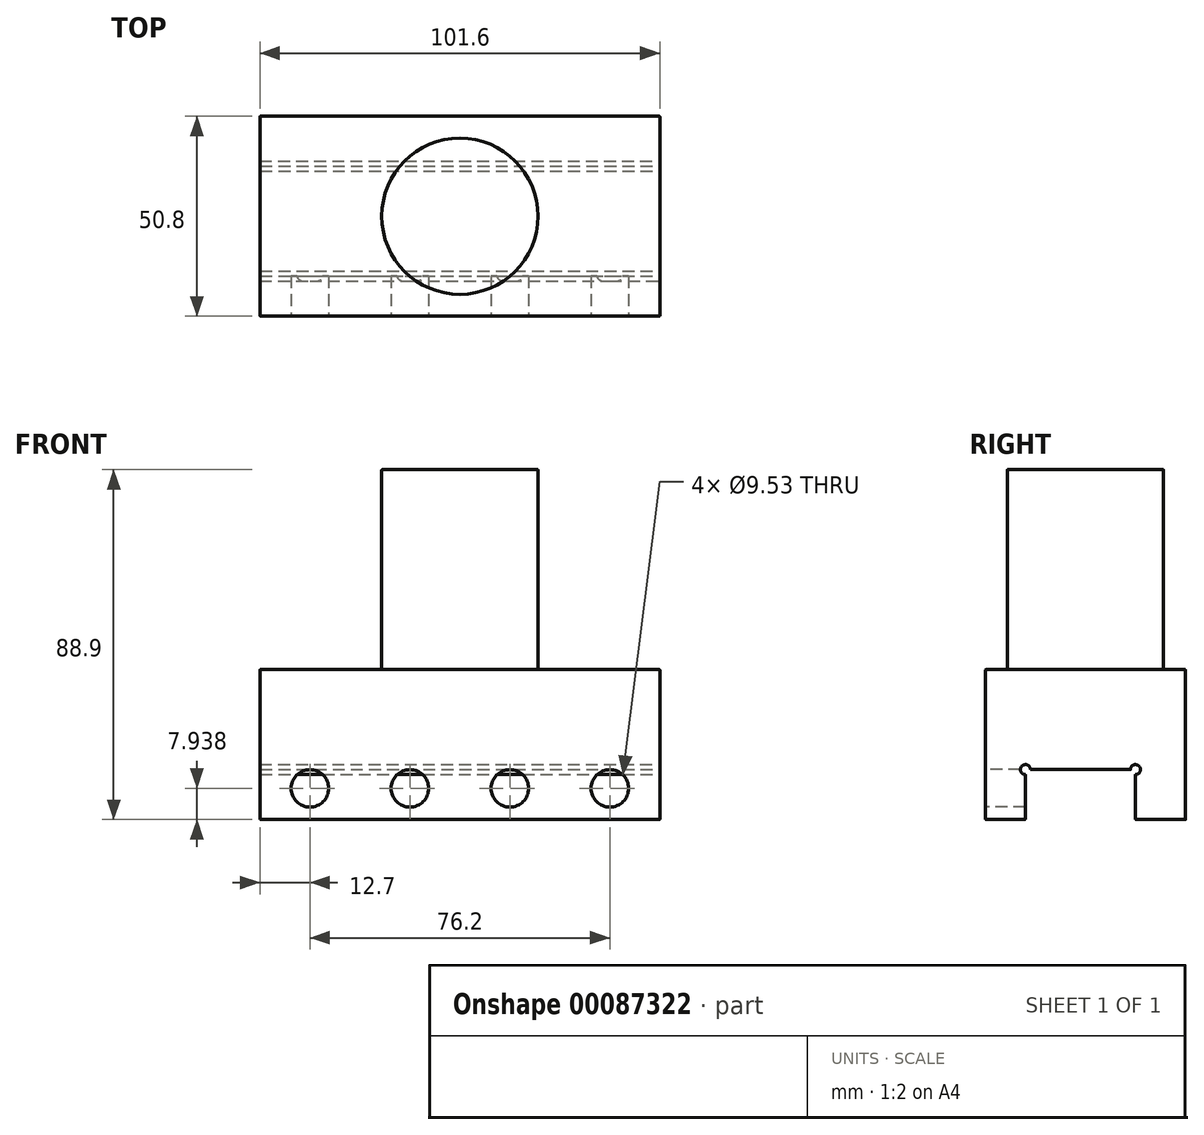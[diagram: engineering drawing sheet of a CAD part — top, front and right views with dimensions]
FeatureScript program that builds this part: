
annotation { "Feature Type Name" : "Feature", "Feature Type Description" : "" }
export const myFeature = defineFeature(function(context is Context, id is Id, definition is map)
    precondition{}
    {
        {
            var Q0;
            Q0=qCreatedBy(makeId("Right.planeOp"),FACE);
            var sketch = newSketch(context, id + "F0", { "sketchPlane" : qUnion([Q0])});
            skLineSegment(sketch, "E0", {"start": v(0, 0) * mm, "end": v(0, 38.1) * mm});
            skLineSegment(sketch, "E1", {"start": v(0, 38.1) * mm, "end": v(50.8, 38.1) * mm});
            skLineSegment(sketch, "E2", {"start": v(50.8, 38.1) * mm, "end": v(50.8, 0) * mm});
            skLineSegment(sketch, "E3", {"start": v(50.8, 0) * mm, "end": v(38.1, 0) * mm});
            skLineSegment(sketch, "E4", {"start": v(38.1, 0) * mm, "end": v(38.1, 11.43) * mm});
            skLineSegment(sketch, "E5", {"start": v(36.83, 12.7) * mm, "end": v(11.43, 12.7) * mm});
            skLineSegment(sketch, "E6", {"start": v(10.16, 11.43) * mm, "end": v(10.16, 0) * mm});
            skLineSegment(sketch, "E7", {"start": v(10.16, 0) * mm, "end": v(0, 0) * mm});
            skArc(sketch, "E8", {"start": v(11.43, 12.7) * mm, "mid": v(9.26, 13.6) * mm, "end": v(10.16, 11.43) * mm});
            skArc(sketch, "E9", {"start": v(38.1, 11.43) * mm, "mid": v(39, 13.6) * mm, "end": v(36.83, 12.7) * mm});
            skSolve(sketch);
        }
        {
            var Q0;
            Q0 = qSketchRegion(id + "F0", true);
            extrude(context, id + "F1", {"entities" : qUnion([Q0]), "oppositeDirection" : true, "depth" : 101.6 * mm});
        }
        {
            var Q0;
            Q0=makeQuery(id+"F1.opExtrude","SWEPT_FACE",FACE,{"disambiguationData":[OSD([sQuery(id+"F0.wireOp",EDGE,"E1")])]});
            var sketch = newSketch(context, id + "F2", { "sketchPlane" : qUnion([Q0])});
            skCircle(sketch, "E10", {"center": v(-50.8, 25.4) * mm, "radius": 19.84 * mm});
            skLineSegment(sketch, "E11", {"start": v(-50.8, 25.4) * mm, "end": v(0, 25.4) * mm});
            skLineSegment(sketch, "E12", {"start": v(-50.8, 25.4) * mm, "end": v(-101.6, 25.4) * mm});
            skPoint(sketch, "E12.endSnap0", {"position": v(-101.6, 25.4) * mm});
            skLineSegment(sketch, "E13", {"start": v(-50.8, 50.8) * mm, "end": v(-50.8, 25.4) * mm});
            skLineSegment(sketch, "E14", {"start": v(-50.8, 25.4) * mm, "end": v(-50.8, 0) * mm});
            skSolve(sketch);
        }
        {
            var Q0;
            Q0 = qSketchRegion(id + "F2", true);
            extrude(context, id + "F3", {"entities" : qUnion([Q0]), "operationType" : NewBodyOperationType.ADD, "depth" : 50.8 * mm});
        }
        {
            var Q0;
            Q0=makeQuery(id+"F1.opExtrude","SWEPT_FACE",FACE,{"disambiguationData":[OSD([sQuery(id+"F0.wireOp",EDGE,"E0")])]});
            var sketch = newSketch(context, id + "F4", { "sketchPlane" : qUnion([Q0])});
            skCircle(sketch, "E15", {"center": v(-12.7, 7.94) * mm, "radius": 4.76 * mm});
            skCircle(sketch, "E16", {"center": v(-38.1, 7.94) * mm, "radius": 4.76 * mm});
            skCircle(sketch, "E17", {"center": v(-63.5, 7.94) * mm, "radius": 4.76 * mm});
            skCircle(sketch, "E18", {"center": v(-88.9, 7.94) * mm, "radius": 4.76 * mm});
            skLineSegment(sketch, "E19", {"start": v(-12.7, 7.94) * mm, "end": v(0, 7.94) * mm});
            skLineSegment(sketch, "E20", {"start": v(-88.9, 7.94) * mm, "end": v(-101.6, 7.94) * mm});
            skSolve(sketch);
        }
        {
            var Q0;
            Q0 = qSketchRegion(id + "F4", true);
            extrude(context, id + "F5", {"entities" : qUnion([Q0]), "operationType" : NewBodyOperationType.REMOVE, "endBound" : BoundingType.UP_TO_NEXT, "oppositeDirection" : true, "depth" : 25.4 * mm});
        }
        {
            var Q0;
            Q0 = qSketchRegion(id + "F4", true);
            extrude(context, id + "F6", {"entities" : qUnion([Q0]), "operationType" : NewBodyOperationType.REMOVE, "endBound" : BoundingType.UP_TO_NEXT, "oppositeDirection" : true, "depth" : 25.4 * mm});
        }
        {
            var Q0;
            Q0=makeQuery(id+"F3.opExtrude","CAP_EDGE",EDGE,{"disambiguationData":[OSD([sQuery(id+"F2.wireOp",EDGE,"E10")])],"isStart":false});
            var Q1;
            Q1=makeQuery(id+"F3.opExtrude","CAP_EDGE",EDGE,{"disambiguationData":[OSD([sQuery(id+"F2.wireOp",EDGE,"E10")])],"isStart":true});
            var Q2;
            Q2=makeQuery(id+"F1.opExtrude","SWEPT_EDGE",EDGE,{"disambiguationData":[OSD([sQuery(id+"F0.wireOp",EDGE,"E0"),sQuery(id+"F0.wireOp",EDGE,"E1")])]});
            var Q3;
            Q3=makeQuery(id+"F1.opExtrude","CAP_EDGE",EDGE,{"disambiguationData":[OSD([sQuery(id+"F0.wireOp",EDGE,"E0")])],"isStart":true});
            var Q4;
            Q4=makeQuery(id+"F1.opExtrude","CAP_EDGE",EDGE,{"disambiguationData":[OSD([sQuery(id+"F0.wireOp",EDGE,"E1")])],"isStart":true});
            var Q5;
            Q5=makeQuery(id+"F1.opExtrude","SWEPT_EDGE",EDGE,{"disambiguationData":[OSD([sQuery(id+"F0.wireOp",EDGE,"E1"),sQuery(id+"F0.wireOp",EDGE,"E2")])]});
            var Q6;
            Q6=makeQuery(id+"F1.opExtrude","CAP_EDGE",EDGE,{"disambiguationData":[OSD([sQuery(id+"F0.wireOp",EDGE,"E1")])],"isStart":false});
            var Q7;
            Q7=makeQuery(id+"F1.opExtrude","CAP_EDGE",EDGE,{"disambiguationData":[OSD([sQuery(id+"F0.wireOp",EDGE,"E0")])],"isStart":false});
            var Q8;
            Q8=makeQuery(id+"F1.opExtrude","SWEPT_EDGE",EDGE,{"disambiguationData":[OSD([sQuery(id+"F0.wireOp",EDGE,"E0"),sQuery(id+"F0.wireOp",EDGE,"E7")])]});
            var Q9;
            Q9=makeQuery(id+"F1.opExtrude","CAP_EDGE",EDGE,{"disambiguationData":[OSD([sQuery(id+"F0.wireOp",EDGE,"E3")])],"isStart":true});
            var Q10;
            Q10=makeQuery(id+"F1.opExtrude","CAP_EDGE",EDGE,{"disambiguationData":[OSD([sQuery(id+"F0.wireOp",EDGE,"E7")])],"isStart":true});
            var Q11;
            Q11=makeQuery(id+"F1.opExtrude","CAP_EDGE",EDGE,{"disambiguationData":[OSD([sQuery(id+"F0.wireOp",EDGE,"E2")])],"isStart":true});
            var Q12;
            Q12=makeQuery(id+"F1.opExtrude","CAP_EDGE",EDGE,{"disambiguationData":[OSD([sQuery(id+"F0.wireOp",EDGE,"E5")])],"isStart":true});
            var Q13;
            Q13=makeQuery(id+"F1.opExtrude","CAP_EDGE",EDGE,{"disambiguationData":[OSD([sQuery(id+"F0.wireOp",EDGE,"E4")])],"isStart":true});
            var Q14;
            Q14=makeQuery(id+"F1.opExtrude","CAP_EDGE",EDGE,{"disambiguationData":[OSD([sQuery(id+"F0.wireOp",EDGE,"E6")])],"isStart":true});
            var Q15;
            Q15=makeQuery(id+"F1.opExtrude","CAP_EDGE",EDGE,{"disambiguationData":[OSD([sQuery(id+"F0.wireOp",EDGE,"E2")])],"isStart":false});
            var Q16;
            Q16=makeQuery(id+"F1.opExtrude","CAP_EDGE",EDGE,{"disambiguationData":[OSD([sQuery(id+"F0.wireOp",EDGE,"E3")])],"isStart":false});
            var Q17;
            Q17=makeQuery(id+"F1.opExtrude","CAP_EDGE",EDGE,{"disambiguationData":[OSD([sQuery(id+"F0.wireOp",EDGE,"E5")])],"isStart":false});
            var Q18;
            Q18=makeQuery(id+"F1.opExtrude","CAP_EDGE",EDGE,{"disambiguationData":[OSD([sQuery(id+"F0.wireOp",EDGE,"E4")])],"isStart":false});
            var Q19;
            Q19=makeQuery(id+"F1.opExtrude","CAP_EDGE",EDGE,{"disambiguationData":[OSD([sQuery(id+"F0.wireOp",EDGE,"E6")])],"isStart":false});
            var Q20;
            Q20=makeQuery(id+"F1.opExtrude","CAP_EDGE",EDGE,{"disambiguationData":[OSD([sQuery(id+"F0.wireOp",EDGE,"E7")])],"isStart":false});
            var Q21;
            Q21=makeQuery(id+"F1.opExtrude","SWEPT_EDGE",EDGE,{"disambiguationData":[OSD([sQuery(id+"F0.wireOp",EDGE,"E3"),sQuery(id+"F0.wireOp",EDGE,"E4")])]});
            var Q22;
            Q22=makeQuery(id+"F1.opExtrude","SWEPT_EDGE",EDGE,{"disambiguationData":[OSD([sQuery(id+"F0.wireOp",EDGE,"E6"),sQuery(id+"F0.wireOp",EDGE,"E7")])]});
            fillet(context, id + "F7", {"entities" : qUnion([Q0, Q1, Q2, Q3, Q4, Q5, Q6, Q7, Q8, Q9, Q10, Q11, Q12, Q13, Q14, Q15, Q16, Q17, Q18, Q19, Q20, Q21, Q22]), "radius" : 0.13 * mm, "tangentPropagation" : true, "allowEdgeOverflow" : false});
        }
    });
